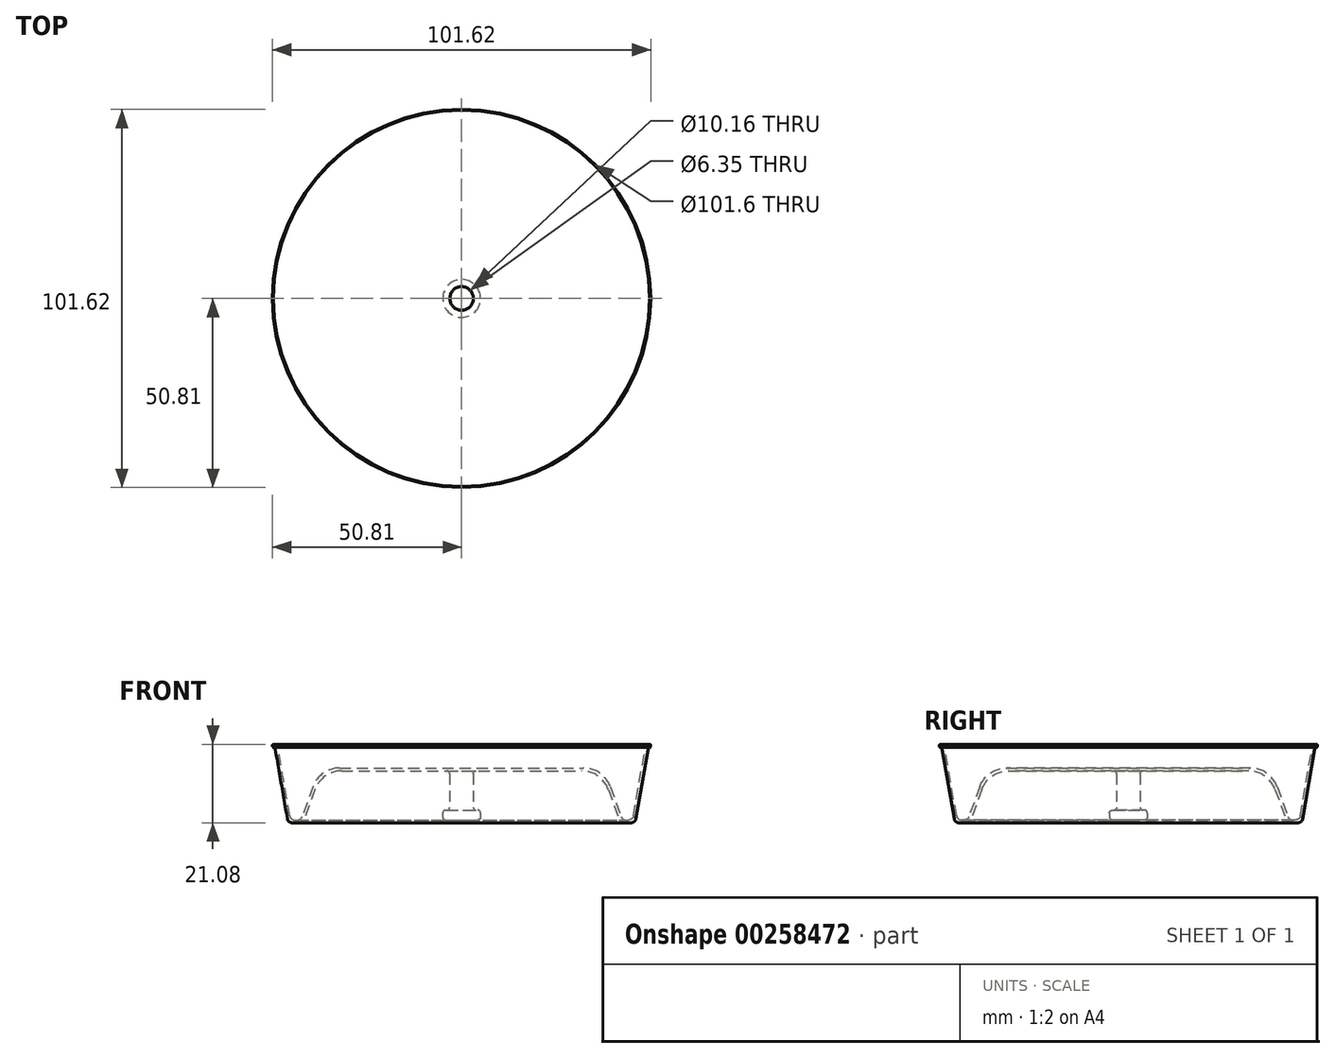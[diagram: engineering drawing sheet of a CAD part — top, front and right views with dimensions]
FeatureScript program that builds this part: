
annotation { "Feature Type Name" : "Feature", "Feature Type Description" : "" }
export const myFeature = defineFeature(function(context is Context, id is Id, definition is map)
    precondition{}
    {
        {
            var Q0;
            Q0=qCreatedBy(makeId("Front.planeOp"),FACE);
            var sketch = newSketch(context, id + "F0", { "sketchPlane" : qUnion([Q0])});
            skLineSegment(sketch, "E0", {"start": v(0, 47.14) * mm, "end": v(0, -44.3) * mm, "construction": true});
            skLineSegment(sketch, "E1", {"start": v(-50.55, 20.32) * mm, "end": v(-50.17, 20.32) * mm});
            skLineSegment(sketch, "E2", {"start": v(-49.42, 19.69) * mm, "end": v(-46.17, 1.05) * mm});
            skLineSegment(sketch, "E3", {"start": v(-44.92, 0) * mm, "end": v(-44.07, 0) * mm});
            skLineSegment(sketch, "E4", {"start": v(-42.88, 0.84) * mm, "end": v(-39.92, 8.95) * mm});
            skLineSegment(sketch, "E5", {"start": v(-32.76, 13.97) * mm, "end": v(-3.17, 13.97) * mm});
            skLineSegment(sketch, "E6", {"start": v(-3.17, 12.45) * mm, "end": v(-3.17, 3.4) * mm});
            skLineSegment(sketch, "E7", {"start": v(-3.94, 2.63) * mm, "end": v(-4.32, 2.63) * mm});
            skLineSegment(sketch, "E8", {"start": v(-5.08, 1.87) * mm, "end": v(-5.08, 0.76) * mm});
            skLineSegment(sketch, "E9", {"start": v(-4.32, 0) * mm, "end": v(0, 0) * mm});
            skLineSegment(sketch, "E10.MirrorCS", {"start": v(46, 0) * mm, "end": v(43.18, 0) * mm});
            skLineSegment(sketch, "E11.0", {"start": v(-32.23, 13.2) * mm, "end": v(-3.94, 13.2) * mm});
            skLineSegment(sketch, "E11.1", {"start": v(-50.81, 19.56) * mm, "end": v(-50.55, 19.56) * mm});
            skLineSegment(sketch, "E11.2", {"start": v(-50.06, 18.93) * mm, "end": v(-46.82, 0.3) * mm});
            skLineSegment(sketch, "E11.3", {"start": v(-45.56, -0.76) * mm, "end": v(-43.54, -0.76) * mm});
            skLineSegment(sketch, "E11.4", {"start": v(-42.34, 0.07) * mm, "end": v(-39.4, 8.2) * mm});
            skLineSegment(sketch, "E12", {"start": v(-50.8, 20.07) * mm, "end": v(-50.8, 19.81) * mm});
            skLineSegment(sketch, "E13", {"start": v(-3.17, 13.97) * mm, "end": v(0, 13.97) * mm});
            skPoint(sketch, "E14.MirrorCS.end.orphan", {"position": v(5.08, 0) * mm});
            skPoint(sketch, "E14.MirrorCS.start.orphan", {"position": v(5.08, 2.63) * mm});
            skPoint(sketch, "E15.MirrorCS.start.orphan", {"position": v(3.18, 2.63) * mm});
            skPoint(sketch, "E16.MirrorCS.start.orphan", {"position": v(3.18, 13.97) * mm});
            skPoint(sketch, "E17.MirrorCS.start.orphan", {"position": v(38.1, 13.97) * mm});
            skPoint(sketch, "E18.MirrorCS.start.orphan", {"position": v(43.18, 0) * mm});
            skPoint(sketch, "E19.MirrorCS.end.orphan", {"position": v(46, 0) * mm});
            skPoint(sketch, "E19.MirrorCS.start.orphan", {"position": v(49.53, 20.32) * mm});
            skPoint(sketch, "E20.MirrorCS.start.orphan", {"position": v(50.8, 20.32) * mm});
            skPoint(sketch, "E21.MirrorCS.end.orphan", {"position": v(0, 0) * mm});
            skPoint(sketch, "E22.visualSharp", {"position": v(-37.57, 13.2) * mm});
            skArc(sketch, "E22.filletArc", {"start": v(-32.23, 13.2) * mm, "mid": v(-36.6, 11.83) * mm, "end": v(-39.4, 8.2) * mm});
            skPoint(sketch, "E23.visualSharp", {"position": v(-38.1, 13.97) * mm});
            skArc(sketch, "E23.filletArc", {"start": v(-32.76, 13.97) * mm, "mid": v(-37.13, 12.6) * mm, "end": v(-39.92, 8.95) * mm});
            skPoint(sketch, "E24.visualSharp", {"position": v(-43.18, 0) * mm});
            skArc(sketch, "E24.filletArc", {"start": v(-44.07, 0) * mm, "mid": v(-43.34, 0.23) * mm, "end": v(-42.88, 0.84) * mm});
            skPoint(sketch, "E25.visualSharp", {"position": v(-42.65, -0.76) * mm});
            skArc(sketch, "E25.filletArc", {"start": v(-43.54, -0.76) * mm, "mid": v(-42.8, -0.53) * mm, "end": v(-42.34, 0.07) * mm});
            skPoint(sketch, "E26.visualSharp", {"position": v(-46, 0) * mm});
            skArc(sketch, "E26.filletArc", {"start": v(-46.17, 1.05) * mm, "mid": v(-45.74, 0.3) * mm, "end": v(-44.92, 0) * mm});
            skPoint(sketch, "E27.visualSharp", {"position": v(-46.63, -0.76) * mm});
            skArc(sketch, "E27.filletArc", {"start": v(-46.82, 0.3) * mm, "mid": v(-46.38, -0.46) * mm, "end": v(-45.56, -0.76) * mm});
            skPoint(sketch, "E28.visualSharp", {"position": v(-3.17, 13.2) * mm});
            skArc(sketch, "E28.filletArc", {"start": v(-3.17, 12.45) * mm, "mid": v(-3.4, 12.98) * mm, "end": v(-3.94, 13.2) * mm});
            skPoint(sketch, "E29.visualSharp", {"position": v(-3.17, 2.63) * mm});
            skArc(sketch, "E29.filletArc", {"start": v(-3.94, 2.63) * mm, "mid": v(-3.4, 2.86) * mm, "end": v(-3.17, 3.4) * mm});
            skPoint(sketch, "E30.visualSharp", {"position": v(-5.08, 2.63) * mm});
            skArc(sketch, "E30.filletArc", {"start": v(-4.32, 2.63) * mm, "mid": v(-4.86, 2.41) * mm, "end": v(-5.08, 1.87) * mm});
            skPoint(sketch, "E31.visualSharp", {"position": v(-5.08, 0) * mm});
            skArc(sketch, "E31.filletArc", {"start": v(-5.08, 0.76) * mm, "mid": v(-4.86, 0.22) * mm, "end": v(-4.32, 0) * mm});
            skPoint(sketch, "E32.visualSharp", {"position": v(-49.53, 20.32) * mm});
            skArc(sketch, "E32.filletArc", {"start": v(-49.42, 19.69) * mm, "mid": v(-49.68, 20.14) * mm, "end": v(-50.17, 20.32) * mm});
            skArc(sketch, "E33.filletArc", {"start": v(-50.06, 18.93) * mm, "mid": v(-50.32, 19.38) * mm, "end": v(-50.81, 19.56) * mm});
            skPoint(sketch, "E34.visualSharp", {"position": v(-50.8, 20.32) * mm});
            skArc(sketch, "E34.filletArc", {"start": v(-50.55, 20.32) * mm, "mid": v(-50.73, 20.25) * mm, "end": v(-50.8, 20.07) * mm});
            skPoint(sketch, "E35.visualSharp", {"position": v(-50.8, 19.56) * mm});
            skArc(sketch, "E35.filletArc", {"start": v(-50.8, 19.81) * mm, "mid": v(-50.73, 19.63) * mm, "end": v(-50.55, 19.56) * mm});
            skSolve(sketch);
        }
        {
            var Q0;
            Q0=sQuery(id+"F0.wireOp",EDGE,"E6");
            var Q1;
            Q1=sQuery(id+"F0.wireOp",EDGE,"E28.filletArc");
            var Q2;
            Q2=sQuery(id+"F0.wireOp",EDGE,"E11.0");
            var Q3;
            Q3=sQuery(id+"F0.wireOp",EDGE,"E5");
            var Q4;
            Q4=sQuery(id+"F0.wireOp",EDGE,"E13");
            var Q5;
            Q5=sQuery(id+"F0.wireOp",EDGE,"E23.filletArc");
            var Q6;
            Q6=sQuery(id+"F0.wireOp",EDGE,"E22.filletArc");
            var Q7;
            Q7=sQuery(id+"F0.wireOp",EDGE,"E11.4");
            var Q8;
            Q8=sQuery(id+"F0.wireOp",EDGE,"E4");
            var Q9;
            Q9=sQuery(id+"F0.wireOp",EDGE,"E24.filletArc");
            var Q10;
            Q10=sQuery(id+"F0.wireOp",EDGE,"E25.filletArc");
            var Q11;
            Q11=sQuery(id+"F0.wireOp",EDGE,"E11.3");
            var Q12;
            Q12=sQuery(id+"F0.wireOp",EDGE,"E3");
            var Q13;
            Q13=sQuery(id+"F0.wireOp",EDGE,"E26.filletArc");
            var Q14;
            Q14=sQuery(id+"F0.wireOp",EDGE,"E27.filletArc");
            var Q15;
            Q15=sQuery(id+"F0.wireOp",EDGE,"E11.2");
            var Q16;
            Q16=sQuery(id+"F0.wireOp",EDGE,"E2");
            var Q17;
            Q17=sQuery(id+"F0.wireOp",EDGE,"E32.filletArc");
            var Q18;
            Q18=sQuery(id+"F0.wireOp",EDGE,"E33.filletArc");
            var Q19;
            Q19=sQuery(id+"F0.wireOp",EDGE,"E11.1");
            var Q20;
            Q20=sQuery(id+"F0.wireOp",EDGE,"E1");
            var Q21;
            Q21=sQuery(id+"F0.wireOp",EDGE,"E12");
            var Q22;
            Q22=sQuery(id+"F0.wireOp",EDGE,"E34.filletArc");
            var Q23;
            Q23=sQuery(id+"F0.wireOp",EDGE,"E35.filletArc");
            var Q24;
            Q24=sQuery(id+"F0.wireOp",EDGE,"E29.filletArc");
            var Q25;
            Q25=sQuery(id+"F0.wireOp",EDGE,"E7");
            var Q26;
            Q26=sQuery(id+"F0.wireOp",EDGE,"E30.filletArc");
            var Q27;
            Q27=sQuery(id+"F0.wireOp",EDGE,"E8");
            var Q28;
            Q28=sQuery(id+"F0.wireOp",EDGE,"E31.filletArc");
            var Q29;
            Q29=sQuery(id+"F0.wireOp",EDGE,"E9");
            var Q30;
            Q30=sQuery(id+"F0.wireOp",EDGE,"E0");
            revolve(context, id + "F1", {"bodyType" : ToolBodyType.SURFACE, "operationType" : NewBodyOperationType.ADD, "surfaceEntities" : qUnion([Q0, Q1, Q2, Q3, Q4, Q5, Q6, Q7, Q8, Q9, Q10, Q11, Q12, Q13, Q14, Q15, Q16, Q17, Q18, Q19, Q20, Q21, Q22, Q23, Q24, Q25, Q26, Q27, Q28, Q29]), "axis" : qUnion([Q30]), "revolveType" : RevolveType.FULL});
        }
    });
